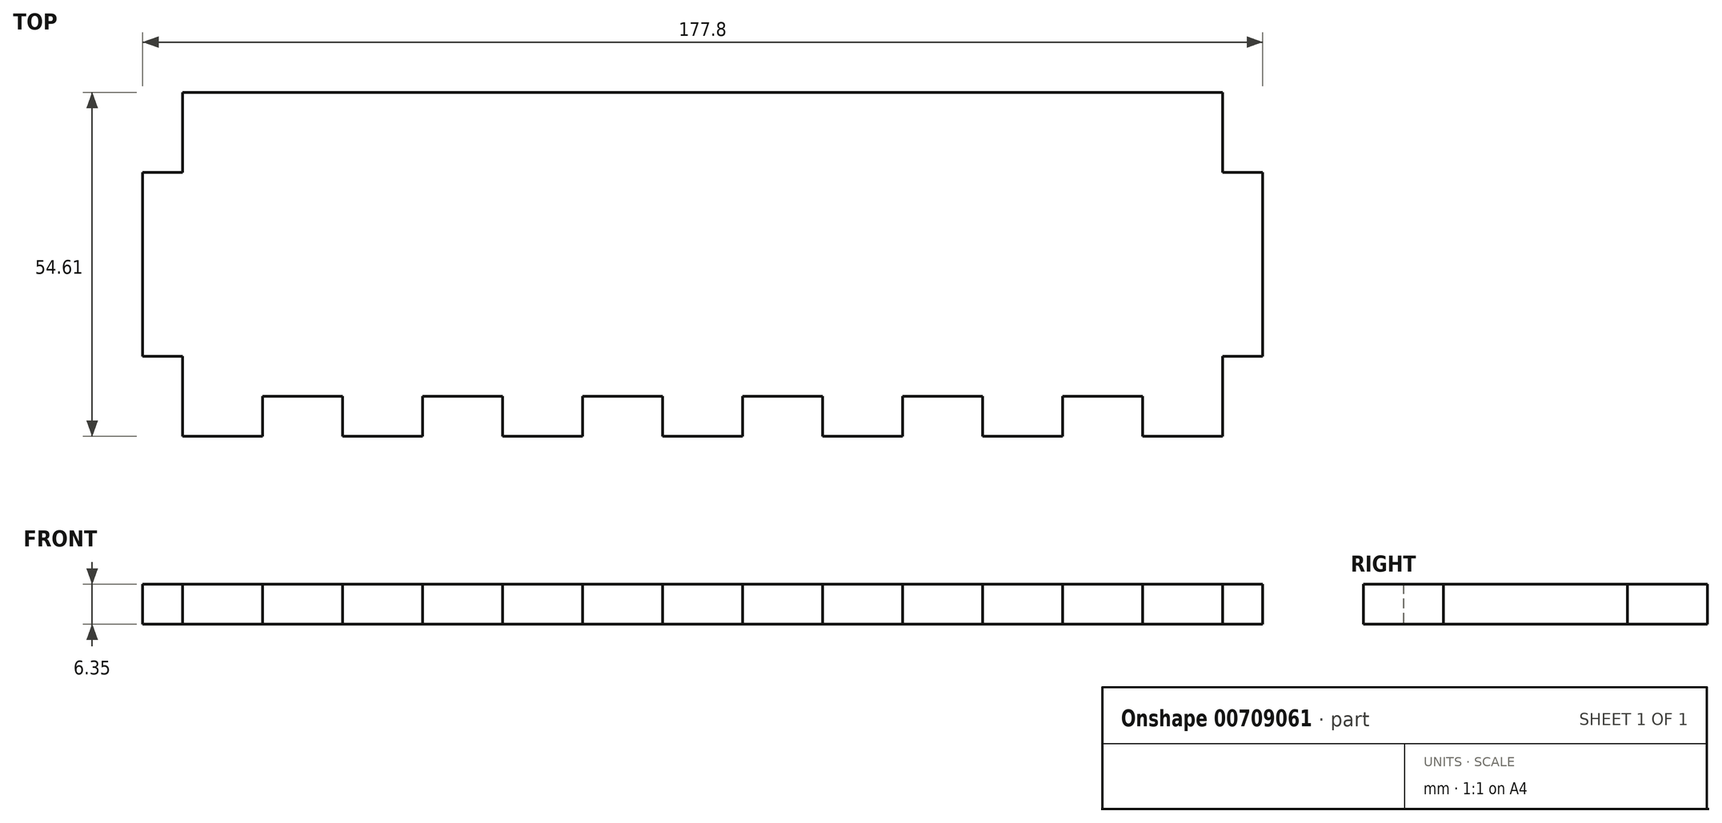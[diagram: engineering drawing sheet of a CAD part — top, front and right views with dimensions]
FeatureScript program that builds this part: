
annotation { "Feature Type Name" : "Feature", "Feature Type Description" : "" }
export const myFeature = defineFeature(function(context is Context, id is Id, definition is map)
    precondition{}
    {
        {
            var Q0;
            Q0=qCreatedBy(makeId("Top.planeOp"),FACE);
            var sketch = newSketch(context, id + "F0", { "sketchPlane" : qUnion([Q0])});
            skLineSegment(sketch, "E0.bottom", {"start": v(6.35, 0) * mm, "end": v(171.45, 0) * mm});
            skLineSegment(sketch, "E0.top", {"start": v(6.35, -54.6) * mm, "end": v(19.05, -54.6) * mm});
            skLineSegment(sketch, "E0.left", {"start": v(0, -12.7) * mm, "end": v(0, -41.9) * mm});
            skLineSegment(sketch, "E1", {"start": v(19.05, -54.61) * mm, "end": v(19.05, -48.26) * mm});
            skLineSegment(sketch, "E2", {"start": v(19.05, -48.26) * mm, "end": v(31.75, -48.26) * mm});
            skLineSegment(sketch, "E3", {"start": v(31.75, -48.26) * mm, "end": v(31.75, -54.61) * mm});
            skLineSegment(sketch, "E4", {"start": v(31.75, -54.61) * mm, "end": v(44.45, -54.61) * mm});
            skLineSegment(sketch, "E5", {"start": v(44.45, -54.61) * mm, "end": v(44.45, -48.26) * mm});
            skLineSegment(sketch, "E6", {"start": v(44.45, -48.26) * mm, "end": v(57.15, -48.26) * mm});
            skLineSegment(sketch, "E7", {"start": v(57.15, -48.26) * mm, "end": v(57.15, -54.61) * mm});
            skLineSegment(sketch, "E8", {"start": v(57.15, -54.61) * mm, "end": v(69.85, -54.61) * mm});
            skLineSegment(sketch, "E9", {"start": v(69.85, -54.61) * mm, "end": v(69.85, -48.26) * mm});
            skLineSegment(sketch, "E10", {"start": v(69.85, -48.26) * mm, "end": v(82.55, -48.26) * mm});
            skLineSegment(sketch, "E11", {"start": v(82.55, -48.26) * mm, "end": v(82.55, -54.61) * mm});
            skLineSegment(sketch, "E12.trimOffspring", {"start": v(31.75, -54.6) * mm, "end": v(44.45, -54.61) * mm});
            skLineSegment(sketch, "E13.trimOffspring", {"start": v(82.55, -54.61) * mm, "end": v(95.25, -54.61) * mm});
            skLineSegment(sketch, "E14", {"start": v(95.25, -54.61) * mm, "end": v(95.25, -48.26) * mm});
            skLineSegment(sketch, "E15", {"start": v(95.25, -48.26) * mm, "end": v(107.95, -48.26) * mm});
            skLineSegment(sketch, "E16", {"start": v(107.95, -48.26) * mm, "end": v(107.95, -54.61) * mm});
            skLineSegment(sketch, "E17", {"start": v(107.95, -54.61) * mm, "end": v(120.65, -54.61) * mm});
            skLineSegment(sketch, "E18", {"start": v(120.65, -54.61) * mm, "end": v(120.65, -48.26) * mm});
            skLineSegment(sketch, "E19", {"start": v(120.65, -48.26) * mm, "end": v(133.35, -48.26) * mm});
            skLineSegment(sketch, "E20", {"start": v(133.35, -48.26) * mm, "end": v(133.35, -54.61) * mm});
            skLineSegment(sketch, "E21", {"start": v(133.35, -54.61) * mm, "end": v(146.05, -54.61) * mm});
            skLineSegment(sketch, "E22", {"start": v(146.05, -54.61) * mm, "end": v(146.05, -48.26) * mm});
            skLineSegment(sketch, "E23", {"start": v(146.05, -48.26) * mm, "end": v(158.75, -48.26) * mm});
            skLineSegment(sketch, "E24", {"start": v(158.75, -48.26) * mm, "end": v(158.75, -54.61) * mm});
            skLineSegment(sketch, "E25.trimOffspring", {"start": v(158.75, -54.61) * mm, "end": v(171.45, -54.61) * mm});
            skLineSegment(sketch, "E26", {"start": v(6.35, -54.6) * mm, "end": v(6.35, -41.9) * mm});
            skLineSegment(sketch, "E27", {"start": v(6.35, -41.9) * mm, "end": v(0, -41.9) * mm});
            skLineSegment(sketch, "E28", {"start": v(0, -41.9) * mm, "end": v(0, -12.7) * mm});
            skLineSegment(sketch, "E29", {"start": v(0, -12.7) * mm, "end": v(6.35, -12.7) * mm});
            skLineSegment(sketch, "E30", {"start": v(6.35, -12.7) * mm, "end": v(6.35, 0) * mm});
            skPoint(sketch, "E31.orphan", {"position": v(0, 0) * mm});
            skPoint(sketch, "E32.orphan", {"position": v(0, -54.6) * mm});
            skLineSegment(sketch, "E33", {"start": v(88.9, -54.61) * mm, "end": v(88.9, -29.7) * mm, "construction": true});
            skLineSegment(sketch, "E34.MirrorCS", {"start": v(171.45, -12.7) * mm, "end": v(171.45, 0) * mm});
            skLineSegment(sketch, "E35.MirrorCS", {"start": v(177.8, -12.7) * mm, "end": v(171.45, -12.7) * mm});
            skLineSegment(sketch, "E36.MirrorCS", {"start": v(177.8, -12.7) * mm, "end": v(177.8, -41.9) * mm});
            skLineSegment(sketch, "E37.MirrorCS", {"start": v(171.45, -41.9) * mm, "end": v(177.8, -41.9) * mm});
            skLineSegment(sketch, "E38.MirrorCS", {"start": v(171.45, -54.6) * mm, "end": v(171.45, -41.9) * mm});
            skPoint(sketch, "E39.orphan", {"position": v(177.8, 0) * mm});
            skSolve(sketch);
        }
        {
            var Q0;
            Q0=makeQuery(id+"F0.imprint","IMPRINT",FACE,{"disambiguationData":[TD([[makeQuery(id+"F0.imprint","IMPRINT",EDGE,{"derivedFrom":sQuery(id+"F0.wireOp",EDGE,"E0.bottom")}),-1.0]])]});
            extrude(context, id + "F1", {"entities" : qUnion([Q0]), "depth" : 6.35 * mm, "offsetDistance" : 25.4 * mm});
        }
    });
